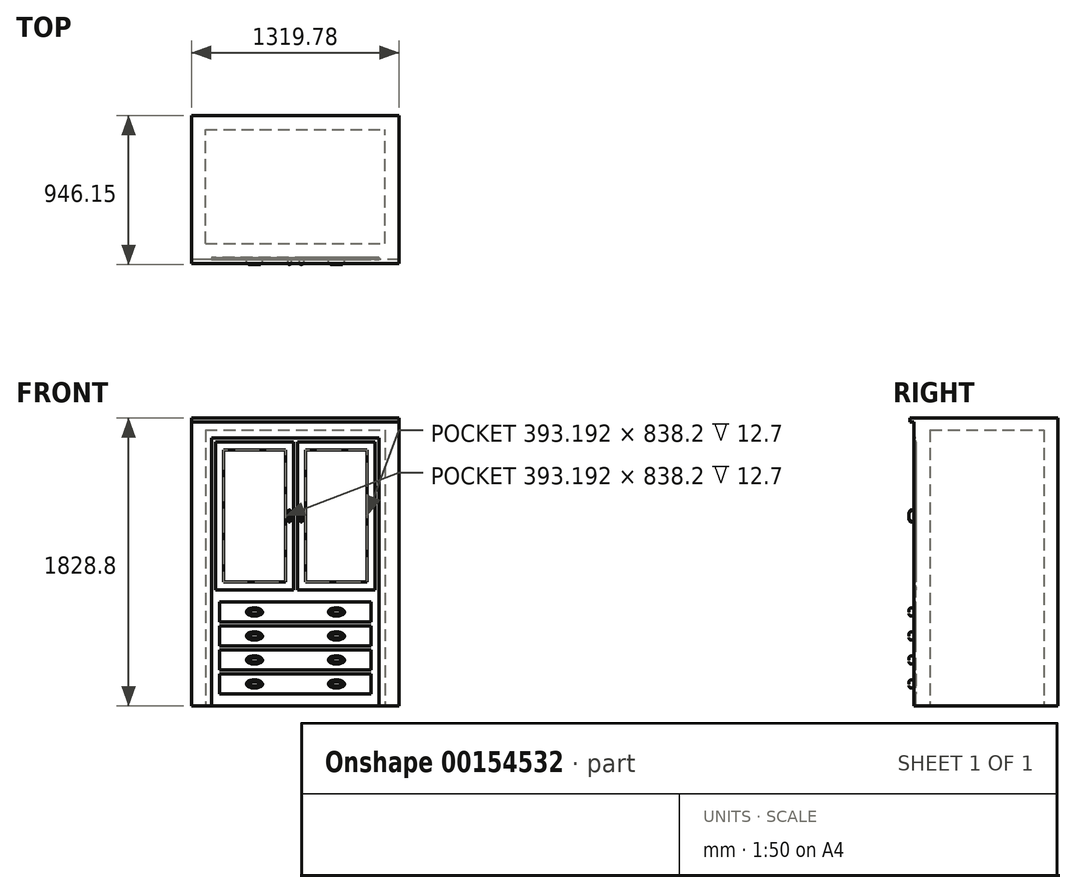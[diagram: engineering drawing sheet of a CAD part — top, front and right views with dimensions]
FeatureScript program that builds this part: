
annotation { "Feature Type Name" : "Feature", "Feature Type Description" : "" }
export const myFeature = defineFeature(function(context is Context, id is Id, definition is map)
    precondition{}
    {
        {
            var Q0;
            Q0=qCreatedBy(makeId("Top.planeOp"),FACE);
            var sketch = newSketch(context, id + "F0", { "sketchPlane" : qUnion([Q0])});
            skLineSegment(sketch, "E0.bottom", {"start": v(659.9, 457.2) * mm, "end": v(-659.9, 457.2) * mm});
            skLineSegment(sketch, "E0.top", {"start": v(659.9, -457.2) * mm, "end": v(-659.9, -457.2) * mm});
            skLineSegment(sketch, "E0.left", {"start": v(659.9, 457.2) * mm, "end": v(659.9, -457.2) * mm});
            skLineSegment(sketch, "E0.right", {"start": v(-659.9, 457.2) * mm, "end": v(-659.9, -457.2) * mm});
            skPoint(sketch, "E0.middle", {"position": v(0, 0) * mm});
            skSolve(sketch);
        }
        {
            var Q0;
            Q0=makeQuery(id+"F0.imprint","IMPRINT",FACE,{"disambiguationData":[TD([[makeQuery(id+"F0.imprint","IMPRINT",EDGE,{"derivedFrom":sQuery(id+"F0.wireOp",EDGE,"E0.bottom")}),1.0]])]});
            extrude(context, id + "F1", {"entities" : qUnion([Q0]), "depth" : 1828.8 * mm});
        }
        {
            var Q0;
            Q0=makeQuery(id+"F1.opExtrude","SWEPT_FACE",FACE,{"disambiguationData":[OSD([sQuery(id+"F0.wireOp",EDGE,"E0.top")])]});
            var sketch = newSketch(context, id + "F2", { "sketchPlane" : qUnion([Q0])});
            skLineSegment(sketch, "E1.bottom", {"start": v(-659.9, 1828.8) * mm, "end": v(659.9, 1828.8) * mm});
            skLineSegment(sketch, "E1.top", {"start": v(-659.9, 0) * mm, "end": v(659.9, 0) * mm});
            skLineSegment(sketch, "E1.left", {"start": v(-659.9, 1828.8) * mm, "end": v(-659.9, 0) * mm});
            skLineSegment(sketch, "E1.right", {"start": v(659.9, 1828.8) * mm, "end": v(659.9, 0) * mm});
            skLineSegment(sketch, "E2", {"start": v(-532.9, 0) * mm, "end": v(-532.9, 1701.8) * mm});
            skLineSegment(sketch, "E3", {"start": v(-532.9, 1701.8) * mm, "end": v(532.9, 1701.8) * mm});
            skLineSegment(sketch, "E4", {"start": v(532.9, 1701.8) * mm, "end": v(532.9, 0) * mm});
            skLineSegment(sketch, "E5.bottom", {"start": v(-482.1, 203.2) * mm, "end": v(482.1, 203.2) * mm});
            skLineSegment(sketch, "E5.top", {"start": v(-482.1, 76.2) * mm, "end": v(482.1, 76.2) * mm});
            skLineSegment(sketch, "E5.left", {"start": v(-482.1, 203.2) * mm, "end": v(-482.1, 76.2) * mm});
            skLineSegment(sketch, "E5.right", {"start": v(482.1, 203.2) * mm, "end": v(482.1, 76.2) * mm});
            skLineSegment(sketch, "E6.bottom", {"start": v(482.1, 228.6) * mm, "end": v(-482.1, 228.6) * mm});
            skLineSegment(sketch, "E6.top", {"start": v(482.1, 355.6) * mm, "end": v(-482.1, 355.6) * mm});
            skLineSegment(sketch, "E6.left", {"start": v(482.1, 228.6) * mm, "end": v(482.1, 355.6) * mm});
            skLineSegment(sketch, "E6.right", {"start": v(-482.1, 228.6) * mm, "end": v(-482.1, 355.6) * mm});
            skLineSegment(sketch, "E7.bottom", {"start": v(-482.1, 381) * mm, "end": v(482.1, 381) * mm});
            skLineSegment(sketch, "E7.top", {"start": v(-482.1, 508) * mm, "end": v(482.1, 508) * mm});
            skLineSegment(sketch, "E7.left", {"start": v(-482.1, 381) * mm, "end": v(-482.1, 508) * mm});
            skLineSegment(sketch, "E7.right", {"start": v(482.1, 381) * mm, "end": v(482.1, 508) * mm});
            skLineSegment(sketch, "E8.bottom", {"start": v(482.1, 533.4) * mm, "end": v(-482.1, 533.4) * mm});
            skLineSegment(sketch, "E8.top", {"start": v(482.1, 660.4) * mm, "end": v(-482.1, 660.4) * mm});
            skLineSegment(sketch, "E8.left", {"start": v(482.1, 533.4) * mm, "end": v(482.1, 660.4) * mm});
            skLineSegment(sketch, "E8.right", {"start": v(-482.1, 533.4) * mm, "end": v(-482.1, 660.4) * mm});
            skLineSegment(sketch, "E9", {"start": v(-293.53, 203.2) * mm, "end": v(-293.53, 228.6) * mm, "construction": true});
            skLineSegment(sketch, "E10", {"start": v(-289.92, 355.6) * mm, "end": v(-289.92, 381) * mm, "construction": true});
            skLineSegment(sketch, "E11", {"start": v(-270.69, 508) * mm, "end": v(-270.69, 533.4) * mm, "construction": true});
            skLineSegment(sketch, "E12.bottom", {"start": v(-507.5, 1676.4) * mm, "end": v(-12.7, 1676.4) * mm});
            skLineSegment(sketch, "E12.top", {"start": v(-507.5, 736.6) * mm, "end": v(-12.7, 736.6) * mm});
            skLineSegment(sketch, "E12.left", {"start": v(-507.5, 1676.4) * mm, "end": v(-507.5, 736.6) * mm});
            skLineSegment(sketch, "E12.right", {"start": v(-12.7, 1676.4) * mm, "end": v(-12.7, 736.6) * mm});
            skLineSegment(sketch, "E13.bottom", {"start": v(507.5, 1676.4) * mm, "end": v(12.7, 1676.4) * mm});
            skLineSegment(sketch, "E13.top", {"start": v(507.5, 736.6) * mm, "end": v(12.7, 736.6) * mm});
            skLineSegment(sketch, "E13.left", {"start": v(507.5, 1676.4) * mm, "end": v(507.5, 736.6) * mm});
            skLineSegment(sketch, "E13.right", {"start": v(12.7, 1676.4) * mm, "end": v(12.7, 736.6) * mm});
            skLineSegment(sketch, "E14.0", {"start": v(-456.7, 1625.6) * mm, "end": v(-63.5, 1625.6) * mm});
            skLineSegment(sketch, "E14.1", {"start": v(-456.7, 1625.6) * mm, "end": v(-456.7, 787.4) * mm});
            skLineSegment(sketch, "E14.2", {"start": v(-456.7, 787.4) * mm, "end": v(-63.5, 787.4) * mm});
            skLineSegment(sketch, "E14.3", {"start": v(-63.5, 1625.6) * mm, "end": v(-63.5, 787.4) * mm});
            skLineSegment(sketch, "E15.0", {"start": v(456.7, 1625.6) * mm, "end": v(63.5, 1625.6) * mm});
            skLineSegment(sketch, "E15.1", {"start": v(456.7, 1625.6) * mm, "end": v(456.7, 787.4) * mm});
            skLineSegment(sketch, "E15.2", {"start": v(456.7, 787.4) * mm, "end": v(63.5, 787.4) * mm});
            skLineSegment(sketch, "E15.3", {"start": v(63.5, 1625.6) * mm, "end": v(63.5, 787.4) * mm});
            skLineSegment(sketch, "E16", {"start": v(456.7, 1625.6) * mm, "end": v(63.5, 1232.4) * mm});
            skLineSegment(sketch, "E17", {"start": v(456.7, 1403.1) * mm, "end": v(63.5, 1009.9) * mm});
            skLineSegment(sketch, "E18", {"start": v(456.7, 1180.6) * mm, "end": v(63.5, 787.4) * mm});
            skLineSegment(sketch, "E19", {"start": v(63.5, 1625.6) * mm, "end": v(456.7, 1232.4) * mm});
            skLineSegment(sketch, "E20", {"start": v(63.5, 1403.1) * mm, "end": v(456.7, 1009.9) * mm});
            skLineSegment(sketch, "E21", {"start": v(456.7, 787.4) * mm, "end": v(63.5, 1180.6) * mm});
            skLineSegment(sketch, "E22", {"start": v(221.8, 1390.7) * mm, "end": v(333.05, 1279.45) * mm, "construction": true});
            skLineSegment(sketch, "E23", {"start": v(333.05, 1279.45) * mm, "end": v(444.3, 1168.2) * mm, "construction": true});
            skLineSegment(sketch, "E24", {"start": v(201.12, 1042.98) * mm, "end": v(312.37, 1154.23) * mm, "construction": true});
            skLineSegment(sketch, "E25", {"start": v(312.37, 1154.23) * mm, "end": v(423.62, 1265.48) * mm, "construction": true});
            skLineSegment(sketch, "E26", {"start": v(286, 1625.6) * mm, "end": v(456.7, 1454.91) * mm});
            skLineSegment(sketch, "E27", {"start": v(234.19, 1625.6) * mm, "end": v(63.5, 1454.91) * mm});
            skLineSegment(sketch, "E28", {"start": v(456.7, 958.09) * mm, "end": v(286, 787.4) * mm});
            skLineSegment(sketch, "E29", {"start": v(63.5, 958.09) * mm, "end": v(234.19, 787.4) * mm});
            skLineSegment(sketch, "E30", {"start": v(418.81, 1492.8) * mm, "end": v(307.56, 1381.54) * mm, "construction": true});
            skLineSegment(sketch, "E31", {"start": v(300.94, 1469.85) * mm, "end": v(189.7, 1581.1) * mm, "construction": true});
            skLineSegment(sketch, "E32", {"start": v(319.18, 1043.08) * mm, "end": v(430.43, 931.82) * mm, "construction": true});
            skLineSegment(sketch, "E33", {"start": v(303.47, 940.63) * mm, "end": v(192.21, 829.37) * mm, "construction": true});
            skLineSegment(sketch, "E34", {"start": v(0, 1828.8) * mm, "end": v(0, 1932.77) * mm, "construction": true});
            skPoint(sketch, "E34.endSnap0", {"position": v(0, 1828.8) * mm});
            skLineSegment(sketch, "E35.MirrorCS", {"start": v(-63.5, 1625.6) * mm, "end": v(-456.7, 1232.4) * mm});
            skLineSegment(sketch, "E36.MirrorCS", {"start": v(-234.19, 1625.6) * mm, "end": v(-63.5, 1454.91) * mm});
            skLineSegment(sketch, "E37.MirrorCS", {"start": v(-456.7, 1625.6) * mm, "end": v(-63.5, 1232.4) * mm});
            skLineSegment(sketch, "E38.MirrorCS", {"start": v(-286, 1625.6) * mm, "end": v(-456.7, 1454.91) * mm});
            skLineSegment(sketch, "E39.MirrorCS", {"start": v(-63.5, 1403.1) * mm, "end": v(-456.7, 1009.9) * mm});
            skLineSegment(sketch, "E40.MirrorCS", {"start": v(-456.7, 1403.1) * mm, "end": v(-63.5, 1009.9) * mm});
            skLineSegment(sketch, "E41.MirrorCS", {"start": v(-456.7, 1180.6) * mm, "end": v(-63.5, 787.4) * mm});
            skLineSegment(sketch, "E42.MirrorCS", {"start": v(-456.7, 787.4) * mm, "end": v(-63.5, 1180.6) * mm});
            skLineSegment(sketch, "E43.MirrorCS", {"start": v(-63.5, 958.09) * mm, "end": v(-234.19, 787.4) * mm});
            skLineSegment(sketch, "E44.MirrorCS", {"start": v(-456.7, 958.09) * mm, "end": v(-286, 787.4) * mm});
            skEllipse(sketch, "E45", {"center": v(38.1, 1206.5) * mm, "majorRadius": 38.1 * mm, "minorRadius": 12.7 * mm, "majorAxis": v(0, -1)});
            skEllipse(sketch, "E46", {"center": v(-38.1, 1206.5) * mm, "majorRadius": 38.1 * mm, "minorRadius": 12.7 * mm, "majorAxis": v(0, 1)});
            skLineSegment(sketch, "E47", {"start": v(-63.5, 1206.5) * mm, "end": v(-12.7, 1206.5) * mm, "construction": true});
            skLineSegment(sketch, "E48", {"start": v(12.7, 1206.5) * mm, "end": v(63.5, 1206.5) * mm});
            skLineSegment(sketch, "E49", {"start": v(-260.1, 736.6) * mm, "end": v(-260.1, 533.4) * mm, "construction": true});
            skLineSegment(sketch, "E50", {"start": v(-482.1, 596.9) * mm, "end": v(-260.1, 596.9) * mm, "construction": true});
            skEllipse(sketch, "E51", {"center": v(-260.1, 596.9) * mm, "majorRadius": 50.8 * mm, "minorRadius": 25.4 * mm, "majorAxis": v(1, 0)});
            skLineSegment(sketch, "E52", {"start": v(260.1, 736.6) * mm, "end": v(260.1, 576.82) * mm, "construction": true});
            skEllipse(sketch, "E53.0.1.0", {"center": v(-260.1, 444.5) * mm, "majorRadius": 50.8 * mm, "minorRadius": 25.4 * mm, "majorAxis": v(1, 0)});
            skEllipse(sketch, "E53.0.2.0", {"center": v(-260.1, 292.1) * mm, "majorRadius": 50.8 * mm, "minorRadius": 25.4 * mm, "majorAxis": v(1, 0)});
            skEllipse(sketch, "E53.0.3.0", {"center": v(-260.1, 139.7) * mm, "majorRadius": 50.8 * mm, "minorRadius": 25.4 * mm, "majorAxis": v(1, 0)});
            skEllipse(sketch, "E53.1.0.0", {"center": v(260.6, 596.9) * mm, "majorRadius": 50.8 * mm, "minorRadius": 25.4 * mm, "majorAxis": v(1, 0)});
            skEllipse(sketch, "E53.1.1.0", {"center": v(260.6, 444.5) * mm, "majorRadius": 50.8 * mm, "minorRadius": 25.4 * mm, "majorAxis": v(1, 0)});
            skEllipse(sketch, "E53.1.2.0", {"center": v(260.6, 292.1) * mm, "majorRadius": 50.8 * mm, "minorRadius": 25.4 * mm, "majorAxis": v(1, 0)});
            skEllipse(sketch, "E53.1.3.0", {"center": v(260.6, 139.7) * mm, "majorRadius": 50.8 * mm, "minorRadius": 25.4 * mm, "majorAxis": v(1, 0)});
            skLineSegment(sketch, "E53.direction1", {"start": v(-260.1, 596.9) * mm, "end": v(260.6, 596.9) * mm, "construction": true});
            skLineSegment(sketch, "E53.direction2", {"start": v(-260.1, 596.9) * mm, "end": v(-260.1, 444.5) * mm, "construction": true});
            skSolve(sketch);
        }
        {
            var Q0;
            {var subQ0=sQuery(id+"F2.wireOp",EDGE,"E2");Q0=makeQuery(id+"F2.imprint","IMPRINT",FACE,{"disambiguationData":[TD([[makeQuery(id+"F2.imprint","IMPRINT",EDGE,{"derivedFrom":subQ0}),-1.0]])]});}
            var Q1;
            {var subQ0=sQuery(id+"F2.wireOp",EDGE,"E20");var subQ1=sQuery(id+"F2.wireOp",EDGE,"E15.3");var subQ2=makeQuery(id+"F2.imprint","INTERSECT",VERTEX,{"derivedFrom":[subQ1,subQ0]});Q1=makeQuery(id+"F2.imprint","IMPRINT",FACE,{"disambiguationData":[TD([[makeQuery(id+"F2.imprint","IMPRINT",EDGE,{"disambiguationData":[TD([[subQ2,1.0]])],"derivedFrom":subQ1}),1.0]])]});}
            var Q2;
            {var subQ1=sQuery(id+"F2.wireOp",EDGE,"E15.3");var subQ3=sQuery(id+"F2.wireOp",EDGE,"E27");var subQ4=makeQuery(id+"F2.imprint","INTERSECT",VERTEX,{"derivedFrom":[subQ1,subQ3]});Q2=makeQuery(id+"F2.imprint","IMPRINT",FACE,{"disambiguationData":[TD([[makeQuery(id+"F2.imprint","IMPRINT",EDGE,{"disambiguationData":[TD([[subQ4,1.0]])],"derivedFrom":subQ3}),-1.0]])]});}
            var Q3;
            {var subQ1=sQuery(id+"F2.wireOp",EDGE,"E15.0");var subQ3=sQuery(id+"F2.wireOp",EDGE,"E27");var subQ4=makeQuery(id+"F2.imprint","INTERSECT",VERTEX,{"derivedFrom":[subQ1,subQ3]});Q3=makeQuery(id+"F2.imprint","IMPRINT",FACE,{"disambiguationData":[TD([[makeQuery(id+"F2.imprint","IMPRINT",EDGE,{"disambiguationData":[TD([[subQ4,-1.0]])],"derivedFrom":subQ3}),-1.0]])]});}
            var Q4;
            {var subQ0=sQuery(id+"F2.wireOp",EDGE,"E26");var subQ1=sQuery(id+"F2.wireOp",EDGE,"E15.0");var subQ2=makeQuery(id+"F2.imprint","INTERSECT",VERTEX,{"derivedFrom":[subQ1,subQ0]});Q4=makeQuery(id+"F2.imprint","IMPRINT",FACE,{"disambiguationData":[TD([[makeQuery(id+"F2.imprint","IMPRINT",EDGE,{"disambiguationData":[TD([[subQ2,-1.0]])],"derivedFrom":subQ1}),1.0]])]});}
            var Q5;
            {var subQ1=sQuery(id+"F2.wireOp",EDGE,"E15.0");var subQ3=sQuery(id+"F2.wireOp",EDGE,"E26");var subQ4=makeQuery(id+"F2.imprint","INTERSECT",VERTEX,{"derivedFrom":[subQ1,subQ3]});Q5=makeQuery(id+"F2.imprint","IMPRINT",FACE,{"disambiguationData":[TD([[makeQuery(id+"F2.imprint","IMPRINT",EDGE,{"disambiguationData":[TD([[subQ4,-1.0]])],"derivedFrom":subQ3}),1.0]])]});}
            var Q6;
            {var subQ1=sQuery(id+"F2.wireOp",EDGE,"E15.1");var subQ3=sQuery(id+"F2.wireOp",EDGE,"E26");var subQ4=makeQuery(id+"F2.imprint","INTERSECT",VERTEX,{"derivedFrom":[subQ1,subQ3]});Q6=makeQuery(id+"F2.imprint","IMPRINT",FACE,{"disambiguationData":[TD([[makeQuery(id+"F2.imprint","IMPRINT",EDGE,{"disambiguationData":[TD([[subQ4,1.0]])],"derivedFrom":subQ3}),1.0]])]});}
            var Q7;
            {var subQ3=sQuery(id+"F2.wireOp",EDGE,"E17");var subQ7=sQuery(id+"F2.wireOp",EDGE,"E15.1");var subQ8=makeQuery(id+"F2.imprint","INTERSECT",VERTEX,{"derivedFrom":[subQ7,subQ3]});Q7=makeQuery(id+"F2.imprint","IMPRINT",FACE,{"disambiguationData":[TD([[makeQuery(id+"F2.imprint","IMPRINT",EDGE,{"disambiguationData":[TD([[subQ8,1.0]])],"derivedFrom":subQ7}),-1.0]])]});}
            var Q8;
            {var subQ0=sQuery(id+"F2.wireOp",EDGE,"E17");var subQ1=sQuery(id+"F2.wireOp",EDGE,"E15.1");var subQ2=makeQuery(id+"F2.imprint","INTERSECT",VERTEX,{"derivedFrom":[subQ1,subQ0]});Q8=makeQuery(id+"F2.imprint","IMPRINT",FACE,{"disambiguationData":[TD([[makeQuery(id+"F2.imprint","IMPRINT",EDGE,{"disambiguationData":[TD([[subQ2,-1.0]])],"derivedFrom":subQ1}),-1.0]])]});}
            var Q9;
            {var subQ1=sQuery(id+"F2.wireOp",EDGE,"E15.1");var subQ7=sQuery(id+"F2.wireOp",EDGE,"E18");var subQ9=makeQuery(id+"F2.imprint","INTERSECT",VERTEX,{"derivedFrom":[subQ1,subQ7]});Q9=makeQuery(id+"F2.imprint","IMPRINT",FACE,{"disambiguationData":[TD([[makeQuery(id+"F2.imprint","IMPRINT",EDGE,{"disambiguationData":[TD([[subQ9,1.0]])],"derivedFrom":subQ1}),-1.0]])]});}
            var Q10;
            {var subQ0=sQuery(id+"F2.wireOp",EDGE,"E19");var subQ1=sQuery(id+"F2.wireOp",EDGE,"E16");var subQ2=makeQuery(id+"F2.imprint","INTERSECT",VERTEX,{"derivedFrom":[subQ1,subQ0]});Q10=makeQuery(id+"F2.imprint","IMPRINT",FACE,{"disambiguationData":[TD([[makeQuery(id+"F2.imprint","IMPRINT",EDGE,{"disambiguationData":[TD([[subQ2,-1.0]])],"derivedFrom":subQ1}),1.0]])]});}
            var Q11;
            {var subQ1=sQuery(id+"F2.wireOp",EDGE,"E16");var subQ7=sQuery(id+"F2.wireOp",EDGE,"E15.3");var subQ8=makeQuery(id+"F2.imprint","INTERSECT",VERTEX,{"derivedFrom":[subQ7,subQ1]});Q11=makeQuery(id+"F2.imprint","IMPRINT",FACE,{"disambiguationData":[TD([[makeQuery(id+"F2.imprint","IMPRINT",EDGE,{"disambiguationData":[TD([[subQ8,-1.0]])],"derivedFrom":subQ7}),1.0]])]});}
            var Q12;
            {var subQ0=sQuery(id+"F2.wireOp",EDGE,"E16");var subQ1=sQuery(id+"F2.wireOp",EDGE,"E15.3");var subQ2=makeQuery(id+"F2.imprint","INTERSECT",VERTEX,{"derivedFrom":[subQ1,subQ0]});Q12=makeQuery(id+"F2.imprint","IMPRINT",FACE,{"disambiguationData":[TD([[makeQuery(id+"F2.imprint","IMPRINT",EDGE,{"disambiguationData":[TD([[subQ2,1.0]])],"derivedFrom":subQ1}),1.0]])]});}
            var Q13;
            {var subQ0=sQuery(id+"F2.wireOp",EDGE,"E18");var subQ1=sQuery(id+"F2.wireOp",EDGE,"E15.1");var subQ2=makeQuery(id+"F2.imprint","INTERSECT",VERTEX,{"derivedFrom":[subQ1,subQ0]});Q13=makeQuery(id+"F2.imprint","IMPRINT",FACE,{"disambiguationData":[TD([[makeQuery(id+"F2.imprint","IMPRINT",EDGE,{"disambiguationData":[TD([[subQ2,-1.0]])],"derivedFrom":subQ1}),-1.0]])]});}
            var Q14;
            {var subQ5=sQuery(id+"F2.wireOp",EDGE,"E20");var subQ6=sQuery(id+"F2.wireOp",EDGE,"E15.1");var subQ7=makeQuery(id+"F2.imprint","INTERSECT",VERTEX,{"derivedFrom":[subQ6,subQ5]});Q14=makeQuery(id+"F2.imprint","IMPRINT",FACE,{"disambiguationData":[TD([[makeQuery(id+"F2.imprint","IMPRINT",EDGE,{"disambiguationData":[TD([[subQ7,-1.0]])],"derivedFrom":subQ6}),-1.0]])]});}
            var Q15;
            {var subQ1=sQuery(id+"F2.wireOp",EDGE,"E15.1");var subQ3=sQuery(id+"F2.wireOp",EDGE,"E28");var subQ4=makeQuery(id+"F2.imprint","INTERSECT",VERTEX,{"derivedFrom":[subQ1,subQ3]});Q15=makeQuery(id+"F2.imprint","IMPRINT",FACE,{"disambiguationData":[TD([[makeQuery(id+"F2.imprint","IMPRINT",EDGE,{"disambiguationData":[TD([[subQ4,-1.0]])],"derivedFrom":subQ3}),1.0]])]});}
            var Q16;
            {var subQ1=sQuery(id+"F2.wireOp",EDGE,"E15.2");var subQ3=sQuery(id+"F2.wireOp",EDGE,"E28");var subQ4=makeQuery(id+"F2.imprint","INTERSECT",VERTEX,{"derivedFrom":[subQ1,subQ3]});Q16=makeQuery(id+"F2.imprint","IMPRINT",FACE,{"disambiguationData":[TD([[makeQuery(id+"F2.imprint","IMPRINT",EDGE,{"disambiguationData":[TD([[subQ4,1.0]])],"derivedFrom":subQ3}),1.0]])]});}
            var Q17;
            {var subQ0=sQuery(id+"F2.wireOp",EDGE,"E28");var subQ1=sQuery(id+"F2.wireOp",EDGE,"E15.2");var subQ2=makeQuery(id+"F2.imprint","INTERSECT",VERTEX,{"derivedFrom":[subQ1,subQ0]});Q17=makeQuery(id+"F2.imprint","IMPRINT",FACE,{"disambiguationData":[TD([[makeQuery(id+"F2.imprint","IMPRINT",EDGE,{"disambiguationData":[TD([[subQ2,-1.0]])],"derivedFrom":subQ1}),-1.0]])]});}
            var Q18;
            {var subQ0=sQuery(id+"F2.wireOp",EDGE,"E20");var subQ1=sQuery(id+"F2.wireOp",EDGE,"E17");var subQ2=makeQuery(id+"F2.imprint","INTERSECT",VERTEX,{"derivedFrom":[subQ1,subQ0]});Q18=makeQuery(id+"F2.imprint","IMPRINT",FACE,{"disambiguationData":[TD([[makeQuery(id+"F2.imprint","IMPRINT",EDGE,{"disambiguationData":[TD([[subQ2,-1.0]])],"derivedFrom":subQ1}),1.0]])]});}
            var Q19;
            {var subQ1=sQuery(id+"F2.wireOp",EDGE,"E17");var subQ7=sQuery(id+"F2.wireOp",EDGE,"E15.3");var subQ8=makeQuery(id+"F2.imprint","INTERSECT",VERTEX,{"derivedFrom":[subQ7,subQ1]});Q19=makeQuery(id+"F2.imprint","IMPRINT",FACE,{"disambiguationData":[TD([[makeQuery(id+"F2.imprint","IMPRINT",EDGE,{"disambiguationData":[TD([[subQ8,-1.0]])],"derivedFrom":subQ7}),1.0]])]});}
            var Q20;
            {var subQ0=sQuery(id+"F2.wireOp",EDGE,"E17");var subQ1=sQuery(id+"F2.wireOp",EDGE,"E15.3");var subQ2=makeQuery(id+"F2.imprint","INTERSECT",VERTEX,{"derivedFrom":[subQ1,subQ0]});Q20=makeQuery(id+"F2.imprint","IMPRINT",FACE,{"disambiguationData":[TD([[makeQuery(id+"F2.imprint","IMPRINT",EDGE,{"disambiguationData":[TD([[subQ2,1.0]])],"derivedFrom":subQ1}),1.0]])]});}
            var Q21;
            {var subQ1=sQuery(id+"F2.wireOp",EDGE,"E15.3");var subQ3=sQuery(id+"F2.wireOp",EDGE,"E29");var subQ4=makeQuery(id+"F2.imprint","INTERSECT",VERTEX,{"derivedFrom":[subQ1,subQ3]});Q21=makeQuery(id+"F2.imprint","IMPRINT",FACE,{"disambiguationData":[TD([[makeQuery(id+"F2.imprint","IMPRINT",EDGE,{"disambiguationData":[TD([[subQ4,-1.0]])],"derivedFrom":subQ3}),-1.0]])]});}
            var Q22;
            {var subQ1=sQuery(id+"F2.wireOp",EDGE,"E15.2");var subQ3=sQuery(id+"F2.wireOp",EDGE,"E29");var subQ4=makeQuery(id+"F2.imprint","INTERSECT",VERTEX,{"derivedFrom":[subQ1,subQ3]});Q22=makeQuery(id+"F2.imprint","IMPRINT",FACE,{"disambiguationData":[TD([[makeQuery(id+"F2.imprint","IMPRINT",EDGE,{"disambiguationData":[TD([[subQ4,1.0]])],"derivedFrom":subQ3}),-1.0]])]});}
            var Q23;
            {var subQ1=sQuery(id+"F2.wireOp",EDGE,"E14.3");var subQ3=sQuery(id+"F2.wireOp",EDGE,"E43.MirrorCS");var subQ4=makeQuery(id+"F2.imprint","INTERSECT",VERTEX,{"derivedFrom":[subQ1,subQ3]});Q23=makeQuery(id+"F2.imprint","IMPRINT",FACE,{"disambiguationData":[TD([[makeQuery(id+"F2.imprint","IMPRINT",EDGE,{"disambiguationData":[TD([[subQ4,-1.0]])],"derivedFrom":subQ3}),1.0]])]});}
            var Q24;
            {var subQ1=sQuery(id+"F2.wireOp",EDGE,"E14.2");var subQ3=sQuery(id+"F2.wireOp",EDGE,"E43.MirrorCS");var subQ4=makeQuery(id+"F2.imprint","INTERSECT",VERTEX,{"derivedFrom":[subQ1,subQ3]});Q24=makeQuery(id+"F2.imprint","IMPRINT",FACE,{"disambiguationData":[TD([[makeQuery(id+"F2.imprint","IMPRINT",EDGE,{"disambiguationData":[TD([[subQ4,1.0]])],"derivedFrom":subQ3}),1.0]])]});}
            var Q25;
            {var subQ0=sQuery(id+"F2.wireOp",EDGE,"E43.MirrorCS");var subQ1=sQuery(id+"F2.wireOp",EDGE,"E14.2");var subQ2=makeQuery(id+"F2.imprint","INTERSECT",VERTEX,{"derivedFrom":[subQ1,subQ0]});Q25=makeQuery(id+"F2.imprint","IMPRINT",FACE,{"disambiguationData":[TD([[makeQuery(id+"F2.imprint","IMPRINT",EDGE,{"disambiguationData":[TD([[subQ2,1.0]])],"derivedFrom":subQ1}),1.0]])]});}
            var Q26;
            {var subQ1=sQuery(id+"F2.wireOp",EDGE,"E40.MirrorCS");var subQ7=sQuery(id+"F2.wireOp",EDGE,"E14.3");var subQ8=makeQuery(id+"F2.imprint","INTERSECT",VERTEX,{"derivedFrom":[subQ7,subQ1]});Q26=makeQuery(id+"F2.imprint","IMPRINT",FACE,{"disambiguationData":[TD([[makeQuery(id+"F2.imprint","IMPRINT",EDGE,{"disambiguationData":[TD([[subQ8,-1.0]])],"derivedFrom":subQ7}),-1.0]])]});}
            var Q27;
            {var subQ0=sQuery(id+"F2.wireOp",EDGE,"E40.MirrorCS");var subQ1=sQuery(id+"F2.wireOp",EDGE,"E14.3");var subQ2=makeQuery(id+"F2.imprint","INTERSECT",VERTEX,{"derivedFrom":[subQ1,subQ0]});Q27=makeQuery(id+"F2.imprint","IMPRINT",FACE,{"disambiguationData":[TD([[makeQuery(id+"F2.imprint","IMPRINT",EDGE,{"disambiguationData":[TD([[subQ2,1.0]])],"derivedFrom":subQ1}),-1.0]])]});}
            var Q28;
            {var subQ0=sQuery(id+"F2.wireOp",EDGE,"E37.MirrorCS");var subQ1=sQuery(id+"F2.wireOp",EDGE,"E14.3");var subQ2=makeQuery(id+"F2.imprint","INTERSECT",VERTEX,{"derivedFrom":[subQ1,subQ0]});Q28=makeQuery(id+"F2.imprint","IMPRINT",FACE,{"disambiguationData":[TD([[makeQuery(id+"F2.imprint","IMPRINT",EDGE,{"disambiguationData":[TD([[subQ2,-1.0]])],"derivedFrom":subQ1}),-1.0]])]});}
            var Q29;
            {var subQ0=sQuery(id+"F2.wireOp",EDGE,"E37.MirrorCS");var subQ1=sQuery(id+"F2.wireOp",EDGE,"E14.3");var subQ2=makeQuery(id+"F2.imprint","INTERSECT",VERTEX,{"derivedFrom":[subQ1,subQ0]});Q29=makeQuery(id+"F2.imprint","IMPRINT",FACE,{"disambiguationData":[TD([[makeQuery(id+"F2.imprint","IMPRINT",EDGE,{"disambiguationData":[TD([[subQ2,1.0]])],"derivedFrom":subQ1}),-1.0]])]});}
            var Q30;
            {var subQ5=sQuery(id+"F2.wireOp",EDGE,"E36.MirrorCS");var subQ6=sQuery(id+"F2.wireOp",EDGE,"E14.3");var subQ7=makeQuery(id+"F2.imprint","INTERSECT",VERTEX,{"derivedFrom":[subQ6,subQ5]});Q30=makeQuery(id+"F2.imprint","IMPRINT",FACE,{"disambiguationData":[TD([[makeQuery(id+"F2.imprint","IMPRINT",EDGE,{"disambiguationData":[TD([[subQ7,-1.0]])],"derivedFrom":subQ6}),-1.0]])]});}
            var Q31;
            {var subQ1=sQuery(id+"F2.wireOp",EDGE,"E14.3");var subQ3=sQuery(id+"F2.wireOp",EDGE,"E36.MirrorCS");var subQ4=makeQuery(id+"F2.imprint","INTERSECT",VERTEX,{"derivedFrom":[subQ1,subQ3]});Q31=makeQuery(id+"F2.imprint","IMPRINT",FACE,{"disambiguationData":[TD([[makeQuery(id+"F2.imprint","IMPRINT",EDGE,{"disambiguationData":[TD([[subQ4,1.0]])],"derivedFrom":subQ3}),1.0]])]});}
            var Q32;
            {var subQ1=sQuery(id+"F2.wireOp",EDGE,"E14.0");var subQ3=sQuery(id+"F2.wireOp",EDGE,"E36.MirrorCS");var subQ4=makeQuery(id+"F2.imprint","INTERSECT",VERTEX,{"derivedFrom":[subQ1,subQ3]});Q32=makeQuery(id+"F2.imprint","IMPRINT",FACE,{"disambiguationData":[TD([[makeQuery(id+"F2.imprint","IMPRINT",EDGE,{"disambiguationData":[TD([[subQ4,-1.0]])],"derivedFrom":subQ3}),1.0]])]});}
            var Q33;
            {var subQ0=sQuery(id+"F2.wireOp",EDGE,"E36.MirrorCS");var subQ1=sQuery(id+"F2.wireOp",EDGE,"E14.0");var subQ2=makeQuery(id+"F2.imprint","INTERSECT",VERTEX,{"derivedFrom":[subQ1,subQ0]});Q33=makeQuery(id+"F2.imprint","IMPRINT",FACE,{"disambiguationData":[TD([[makeQuery(id+"F2.imprint","IMPRINT",EDGE,{"disambiguationData":[TD([[subQ2,1.0]])],"derivedFrom":subQ1}),-1.0]])]});}
            var Q34;
            {var subQ1=sQuery(id+"F2.wireOp",EDGE,"E14.0");var subQ3=sQuery(id+"F2.wireOp",EDGE,"E38.MirrorCS");var subQ4=makeQuery(id+"F2.imprint","INTERSECT",VERTEX,{"derivedFrom":[subQ1,subQ3]});Q34=makeQuery(id+"F2.imprint","IMPRINT",FACE,{"disambiguationData":[TD([[makeQuery(id+"F2.imprint","IMPRINT",EDGE,{"disambiguationData":[TD([[subQ4,-1.0]])],"derivedFrom":subQ3}),-1.0]])]});}
            var Q35;
            {var subQ0=sQuery(id+"F2.wireOp",EDGE,"E38.MirrorCS");var subQ1=sQuery(id+"F2.wireOp",EDGE,"E14.1");var subQ2=makeQuery(id+"F2.imprint","INTERSECT",VERTEX,{"derivedFrom":[subQ1,subQ0]});Q35=makeQuery(id+"F2.imprint","IMPRINT",FACE,{"disambiguationData":[TD([[makeQuery(id+"F2.imprint","IMPRINT",EDGE,{"disambiguationData":[TD([[subQ2,-1.0]])],"derivedFrom":subQ1}),1.0]])]});}
            var Q36;
            {var subQ0=sQuery(id+"F2.wireOp",EDGE,"E37.MirrorCS");var subQ1=sQuery(id+"F2.wireOp",EDGE,"E35.MirrorCS");var subQ2=makeQuery(id+"F2.imprint","INTERSECT",VERTEX,{"derivedFrom":[subQ1,subQ0]});Q36=makeQuery(id+"F2.imprint","IMPRINT",FACE,{"disambiguationData":[TD([[makeQuery(id+"F2.imprint","IMPRINT",EDGE,{"disambiguationData":[TD([[subQ2,-1.0]])],"derivedFrom":subQ1}),1.0]])]});}
            var Q37;
            {var subQ1=sQuery(id+"F2.wireOp",EDGE,"E35.MirrorCS");var subQ5=sQuery(id+"F2.wireOp",EDGE,"E14.1");var subQ6=makeQuery(id+"F2.imprint","INTERSECT",VERTEX,{"derivedFrom":[subQ5,subQ1]});Q37=makeQuery(id+"F2.imprint","IMPRINT",FACE,{"disambiguationData":[TD([[makeQuery(id+"F2.imprint","IMPRINT",EDGE,{"disambiguationData":[TD([[subQ6,-1.0]])],"derivedFrom":subQ5}),1.0]])]});}
            var Q38;
            {var subQ0=sQuery(id+"F2.wireOp",EDGE,"E40.MirrorCS");var subQ1=sQuery(id+"F2.wireOp",EDGE,"E39.MirrorCS");var subQ2=makeQuery(id+"F2.imprint","INTERSECT",VERTEX,{"derivedFrom":[subQ1,subQ0]});Q38=makeQuery(id+"F2.imprint","IMPRINT",FACE,{"disambiguationData":[TD([[makeQuery(id+"F2.imprint","IMPRINT",EDGE,{"disambiguationData":[TD([[subQ2,-1.0]])],"derivedFrom":subQ1}),1.0]])]});}
            var Q39;
            {var subQ5=sQuery(id+"F2.wireOp",EDGE,"E39.MirrorCS");var subQ7=sQuery(id+"F2.wireOp",EDGE,"E14.1");var subQ8=makeQuery(id+"F2.imprint","INTERSECT",VERTEX,{"derivedFrom":[subQ7,subQ5]});Q39=makeQuery(id+"F2.imprint","IMPRINT",FACE,{"disambiguationData":[TD([[makeQuery(id+"F2.imprint","IMPRINT",EDGE,{"disambiguationData":[TD([[subQ8,-1.0]])],"derivedFrom":subQ7}),1.0]])]});}
            var Q40;
            {var subQ1=sQuery(id+"F2.wireOp",EDGE,"E14.1");var subQ3=sQuery(id+"F2.wireOp",EDGE,"E44.MirrorCS");var subQ4=makeQuery(id+"F2.imprint","INTERSECT",VERTEX,{"derivedFrom":[subQ1,subQ3]});Q40=makeQuery(id+"F2.imprint","IMPRINT",FACE,{"disambiguationData":[TD([[makeQuery(id+"F2.imprint","IMPRINT",EDGE,{"disambiguationData":[TD([[subQ4,-1.0]])],"derivedFrom":subQ3}),-1.0]])]});}
            var Q41;
            {var subQ1=sQuery(id+"F2.wireOp",EDGE,"E14.2");var subQ3=sQuery(id+"F2.wireOp",EDGE,"E44.MirrorCS");var subQ4=makeQuery(id+"F2.imprint","INTERSECT",VERTEX,{"derivedFrom":[subQ1,subQ3]});Q41=makeQuery(id+"F2.imprint","IMPRINT",FACE,{"disambiguationData":[TD([[makeQuery(id+"F2.imprint","IMPRINT",EDGE,{"disambiguationData":[TD([[subQ4,1.0]])],"derivedFrom":subQ3}),-1.0]])]});}
            var Q42;
            {var subQ0=sQuery(id+"F2.wireOp",EDGE,"E39.MirrorCS");var subQ1=sQuery(id+"F2.wireOp",EDGE,"E14.1");var subQ2=makeQuery(id+"F2.imprint","INTERSECT",VERTEX,{"derivedFrom":[subQ1,subQ0]});Q42=makeQuery(id+"F2.imprint","IMPRINT",FACE,{"disambiguationData":[TD([[makeQuery(id+"F2.imprint","IMPRINT",EDGE,{"disambiguationData":[TD([[subQ2,1.0]])],"derivedFrom":subQ1}),1.0]])]});}
            var Q43;
            {var subQ0=sQuery(id+"F2.wireOp",EDGE,"E35.MirrorCS");var subQ1=sQuery(id+"F2.wireOp",EDGE,"E14.1");var subQ2=makeQuery(id+"F2.imprint","INTERSECT",VERTEX,{"derivedFrom":[subQ1,subQ0]});Q43=makeQuery(id+"F2.imprint","IMPRINT",FACE,{"disambiguationData":[TD([[makeQuery(id+"F2.imprint","IMPRINT",EDGE,{"disambiguationData":[TD([[subQ2,1.0]])],"derivedFrom":subQ1}),1.0]])]});}
            var Q44;
            {var subQ1=sQuery(id+"F2.wireOp",EDGE,"E14.1");var subQ3=sQuery(id+"F2.wireOp",EDGE,"E38.MirrorCS");var subQ4=makeQuery(id+"F2.imprint","INTERSECT",VERTEX,{"derivedFrom":[subQ1,subQ3]});Q44=makeQuery(id+"F2.imprint","IMPRINT",FACE,{"disambiguationData":[TD([[makeQuery(id+"F2.imprint","IMPRINT",EDGE,{"disambiguationData":[TD([[subQ4,1.0]])],"derivedFrom":subQ3}),-1.0]])]});}
            extrude(context, id + "F3", {"entities" : qUnion([Q0, Q1, Q2, Q3, Q4, Q5, Q6, Q7, Q8, Q9, Q10, Q11, Q12, Q13, Q14, Q15, Q16, Q17, Q18, Q19, Q20, Q21, Q22, Q23, Q24, Q25, Q26, Q27, Q28, Q29, Q30, Q31, Q32, Q33, Q34, Q35, Q36, Q37, Q38, Q39, Q40, Q41, Q42, Q43, Q44]), "operationType" : NewBodyOperationType.REMOVE, "oppositeDirection" : true, "depth" : 12.7 * mm});
        }
        {
            var Q0;
            {var subQ0=sQuery(id+"F2.wireOp",EDGE,"E48");var subQ1=sQuery(id+"F2.wireOp",EDGE,"E45");var subQ2=makeQuery(id+"F2.imprint","INTERSECT",VERTEX,{"disambiguationData":[OD(0.0)],"derivedFrom":[subQ1,subQ0]});Q0=makeQuery(id+"F2.imprint","IMPRINT",FACE,{"disambiguationData":[TD([[makeQuery(id+"F2.imprint","IMPRINT",EDGE,{"disambiguationData":[TD([[subQ2,-1.0]])],"derivedFrom":subQ1}),1.0]])]});}
            var Q1;
            {var subQ0=sQuery(id+"F2.wireOp",EDGE,"E48");var subQ1=sQuery(id+"F2.wireOp",EDGE,"E45");var subQ2=makeQuery(id+"F2.imprint","INTERSECT",VERTEX,{"disambiguationData":[OD(0.0)],"derivedFrom":[subQ1,subQ0]});Q1=makeQuery(id+"F2.imprint","IMPRINT",FACE,{"disambiguationData":[TD([[makeQuery(id+"F2.imprint","IMPRINT",EDGE,{"disambiguationData":[TD([[subQ2,1.0]])],"derivedFrom":subQ1}),1.0]])]});}
            var Q2;
            Q2=makeQuery(id+"F2.imprint","IMPRINT",FACE,{"disambiguationData":[TD([[makeQuery(id+"F2.imprint","IMPRINT",EDGE,{"derivedFrom":sQuery(id+"F2.wireOp",EDGE,"E46")}),1.0]])]});
            var Q3;
            Q3=makeQuery(id+"F2.imprint","IMPRINT",FACE,{"disambiguationData":[TD([[makeQuery(id+"F2.imprint","IMPRINT",EDGE,{"derivedFrom":sQuery(id+"F2.wireOp",EDGE,"E53.1.0.0")}),1.0]])]});
            var Q4;
            Q4=makeQuery(id+"F2.imprint","IMPRINT",FACE,{"disambiguationData":[TD([[makeQuery(id+"F2.imprint","IMPRINT",EDGE,{"derivedFrom":sQuery(id+"F2.wireOp",EDGE,"E51")}),1.0]])]});
            var Q5;
            Q5=makeQuery(id+"F2.imprint","IMPRINT",FACE,{"disambiguationData":[TD([[makeQuery(id+"F2.imprint","IMPRINT",EDGE,{"derivedFrom":sQuery(id+"F2.wireOp",EDGE,"E53.0.1.0")}),1.0]])]});
            var Q6;
            Q6=makeQuery(id+"F2.imprint","IMPRINT",FACE,{"disambiguationData":[TD([[makeQuery(id+"F2.imprint","IMPRINT",EDGE,{"derivedFrom":sQuery(id+"F2.wireOp",EDGE,"E53.1.1.0")}),1.0]])]});
            var Q7;
            Q7=makeQuery(id+"F2.imprint","IMPRINT",FACE,{"disambiguationData":[TD([[makeQuery(id+"F2.imprint","IMPRINT",EDGE,{"derivedFrom":sQuery(id+"F2.wireOp",EDGE,"E53.1.2.0")}),1.0]])]});
            var Q8;
            Q8=makeQuery(id+"F2.imprint","IMPRINT",FACE,{"disambiguationData":[TD([[makeQuery(id+"F2.imprint","IMPRINT",EDGE,{"derivedFrom":sQuery(id+"F2.wireOp",EDGE,"E53.1.3.0")}),1.0]])]});
            var Q9;
            Q9=makeQuery(id+"F2.imprint","IMPRINT",FACE,{"disambiguationData":[TD([[makeQuery(id+"F2.imprint","IMPRINT",EDGE,{"derivedFrom":sQuery(id+"F2.wireOp",EDGE,"E53.0.3.0")}),1.0]])]});
            var Q10;
            Q10=makeQuery(id+"F2.imprint","IMPRINT",FACE,{"disambiguationData":[TD([[makeQuery(id+"F2.imprint","IMPRINT",EDGE,{"derivedFrom":sQuery(id+"F2.wireOp",EDGE,"E53.0.2.0")}),1.0]])]});
            extrude(context, id + "F4", {"entities" : qUnion([Q0, Q1, Q2, Q3, Q4, Q5, Q6, Q7, Q8, Q9, Q10]), "operationType" : NewBodyOperationType.ADD, "depth" : 31.75 * mm});
        }
        {
            var Q0;
            Q0=makeQuery(id+"F4.opExtrude","CAP_EDGE",EDGE,{"disambiguationData":[OSD([sQuery(id+"F2.wireOp",EDGE,"E45")])],"isStart":false});
            var Q1;
            Q1=makeQuery(id+"F4.opExtrude","CAP_FACE",FACE,{"disambiguationData":[OSD([sQuery(id+"F2.wireOp",EDGE,"E46")])],"isStart":false});
            var Q2;
            Q2=makeQuery(id+"F4.opExtrude","CAP_FACE",FACE,{"disambiguationData":[OSD([sQuery(id+"F2.wireOp",EDGE,"E53.1.0.0")])],"isStart":false});
            var Q3;
            Q3=makeQuery(id+"F4.opExtrude","CAP_FACE",FACE,{"disambiguationData":[OSD([sQuery(id+"F2.wireOp",EDGE,"E53.1.1.0")])],"isStart":false});
            var Q4;
            Q4=makeQuery(id+"F4.opExtrude","CAP_FACE",FACE,{"disambiguationData":[OSD([sQuery(id+"F2.wireOp",EDGE,"E51")])],"isStart":false});
            var Q5;
            Q5=makeQuery(id+"F4.opExtrude","CAP_FACE",FACE,{"disambiguationData":[OSD([sQuery(id+"F2.wireOp",EDGE,"E53.0.1.0")])],"isStart":false});
            var Q6;
            Q6=makeQuery(id+"F4.opExtrude","CAP_FACE",FACE,{"disambiguationData":[OSD([sQuery(id+"F2.wireOp",EDGE,"E53.1.2.0")])],"isStart":false});
            var Q7;
            Q7=makeQuery(id+"F4.opExtrude","CAP_FACE",FACE,{"disambiguationData":[OSD([sQuery(id+"F2.wireOp",EDGE,"E53.1.3.0")])],"isStart":false});
            var Q8;
            Q8=makeQuery(id+"F4.opExtrude","CAP_FACE",FACE,{"disambiguationData":[OSD([sQuery(id+"F2.wireOp",EDGE,"E53.0.2.0")])],"isStart":false});
            var Q9;
            Q9=makeQuery(id+"F4.opExtrude","CAP_FACE",FACE,{"disambiguationData":[OSD([sQuery(id+"F2.wireOp",EDGE,"E53.0.3.0")])],"isStart":false});
            fillet(context, id + "F5", {"entities" : qUnion([Q0, Q1, Q2, Q3, Q4, Q5, Q6, Q7, Q8, Q9]), "radius" : 12.7 * mm, "tangentPropagation" : true, "allowEdgeOverflow" : false});
        }
        {
            var Q0;
            Q0=makeQuery(id+"F1.opExtrude","CAP_FACE",FACE,{"disambiguationData":[OSD([sQuery(id+"F0.wireOp",EDGE,"E0.bottom"),sQuery(id+"F0.wireOp",EDGE,"E0.top"),sQuery(id+"F0.wireOp",EDGE,"E0.left"),sQuery(id+"F0.wireOp",EDGE,"E0.right")])],"isStart":true});
            var sketch = newSketch(context, id + "F6", { "sketchPlane" : qUnion([Q0])});
            skLineSegment(sketch, "E54.bottom", {"start": v(-571, 355.6) * mm, "end": v(571, 355.6) * mm});
            skLineSegment(sketch, "E54.top", {"start": v(-571, -368.3) * mm, "end": v(571, -368.3) * mm});
            skLineSegment(sketch, "E54.left", {"start": v(-571, 355.6) * mm, "end": v(-571, -368.3) * mm});
            skLineSegment(sketch, "E54.right", {"start": v(571, 355.6) * mm, "end": v(571, -368.3) * mm});
            skSolve(sketch);
        }
        {
            var Q0;
            Q0=makeQuery(id+"F6.imprint","IMPRINT",FACE,{"disambiguationData":[TD([[makeQuery(id+"F6.imprint","IMPRINT",EDGE,{"derivedFrom":sQuery(id+"F6.wireOp",EDGE,"E54.bottom")}),-1.0]])]});
            extrude(context, id + "F7", {"entities" : qUnion([Q0]), "operationType" : NewBodyOperationType.REMOVE, "oppositeDirection" : true, "depth" : 1752.6 * mm});
        }
        {
            var Q0;
            Q0=makeQuery(id+"F1.opExtrude","CAP_FACE",FACE,{"disambiguationData":[OSD([sQuery(id+"F0.wireOp",EDGE,"E0.bottom"),sQuery(id+"F0.wireOp",EDGE,"E0.top"),sQuery(id+"F0.wireOp",EDGE,"E0.left"),sQuery(id+"F0.wireOp",EDGE,"E0.right")])],"isStart":false});
            var sketch = newSketch(context, id + "F8", { "sketchPlane" : qUnion([Q0])});
            skLineSegment(sketch, "E55.bottom", {"start": v(-659.9, 457.2) * mm, "end": v(659.9, 457.2) * mm});
            skLineSegment(sketch, "E55.top", {"start": v(-659.9, -482.6) * mm, "end": v(659.9, -482.6) * mm});
            skLineSegment(sketch, "E55.left", {"start": v(-659.9, 457.2) * mm, "end": v(-659.9, -482.6) * mm});
            skLineSegment(sketch, "E55.right", {"start": v(659.9, 457.2) * mm, "end": v(659.9, -482.6) * mm});
            skSolve(sketch);
        }
        {
            var Q0;
            Q0 = qSketchRegion(id + "F8", true);
            extrude(context, id + "F9", {"entities" : qUnion([Q0]), "operationType" : NewBodyOperationType.ADD, "oppositeDirection" : true, "depth" : 25.4 * mm});
        }
    });
